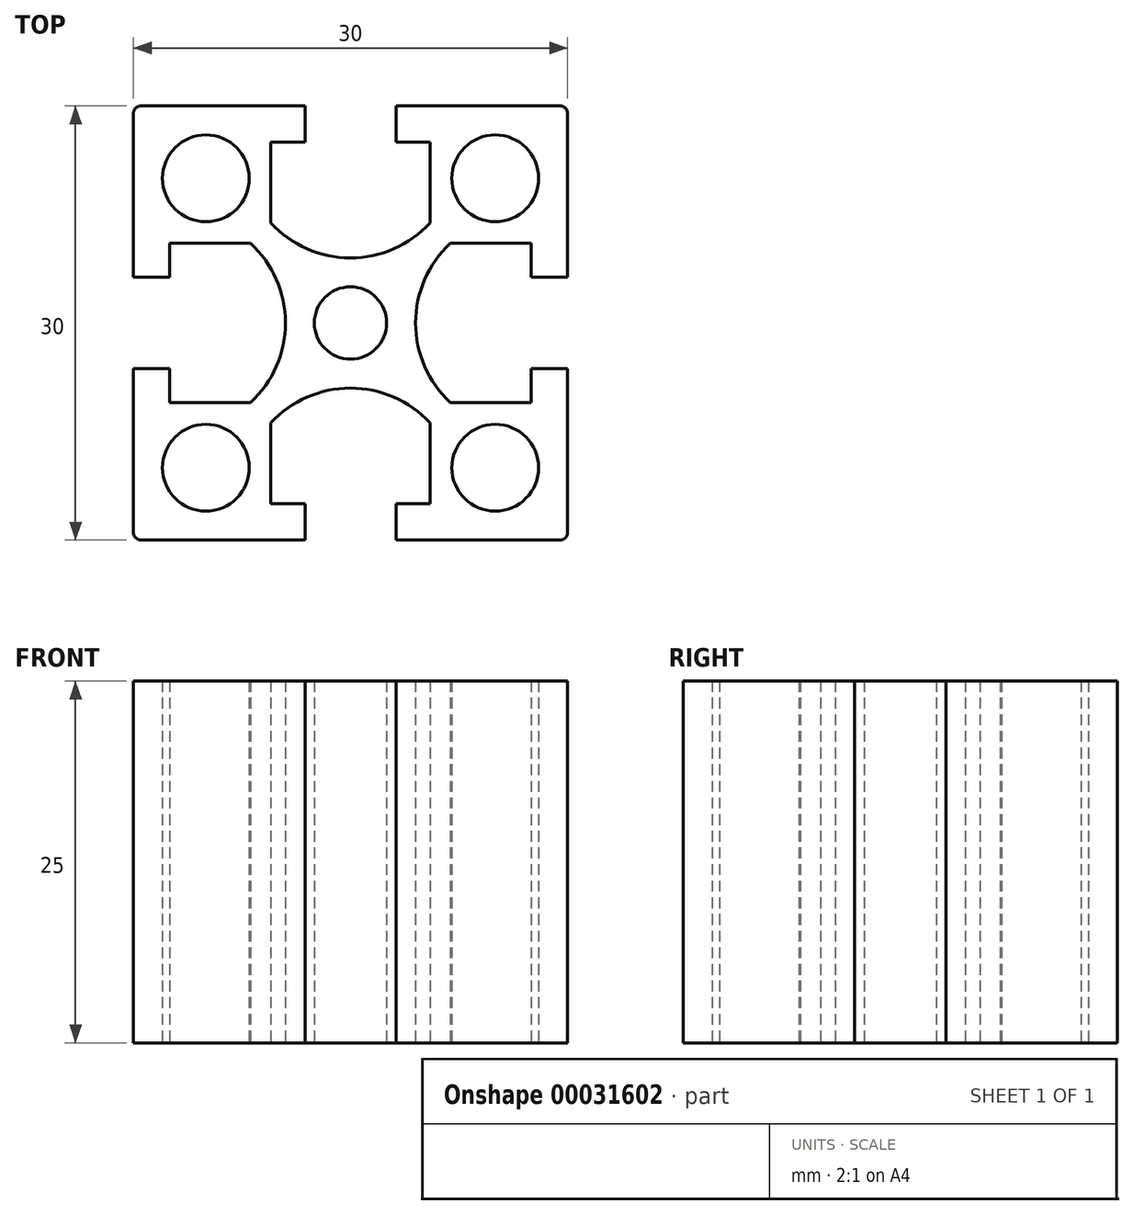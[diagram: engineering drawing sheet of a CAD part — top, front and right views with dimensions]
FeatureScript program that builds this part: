
annotation { "Feature Type Name" : "Feature", "Feature Type Description" : "" }
export const myFeature = defineFeature(function(context is Context, id is Id, definition is map)
    precondition{}
    {
        {
            var Q0;
            Q0=qCreatedBy(makeId("Top.planeOp"),FACE);
            var sketch = newSketch(context, id + "F0", { "sketchPlane" : qUnion([Q0])});
            skCircle(sketch, "E0", {"center": v(0, 0) * mm, "radius": 2.5 * mm});
            skLineSegment(sketch, "E1", {"start": v(0, 0) * mm, "end": v(-15, 0) * mm, "construction": true});
            skLineSegment(sketch, "E2", {"start": v(-15, 0) * mm, "end": v(-15, 15) * mm, "construction": true});
            skLineSegment(sketch, "E3", {"start": v(-15, 15) * mm, "end": v(0, 15) * mm, "construction": true});
            skLineSegment(sketch, "E4", {"start": v(0, 15) * mm, "end": v(0, 0) * mm, "construction": true});
            skLineSegment(sketch, "E5", {"start": v(-15, 15) * mm, "end": v(0, 0) * mm, "construction": true});
            skLineSegment(sketch, "E6", {"start": v(-15, 10) * mm, "end": v(-10, 10) * mm, "construction": true});
            skPoint(sketch, "E7", {"position": v(-15, 3.15) * mm});
            skPoint(sketch, "E8", {"position": v(-15, 5.5) * mm});
            skCircle(sketch, "E9", {"center": v(-10, 10) * mm, "radius": 3 * mm});
            skLineSegment(sketch, "E10", {"start": v(-15, 14.5) * mm, "end": v(-15, 3.15) * mm});
            skLineSegment(sketch, "E11", {"start": v(-15, 3.15) * mm, "end": v(-12.5, 3.15) * mm});
            skLineSegment(sketch, "E12", {"start": v(-12.5, 3.15) * mm, "end": v(-12.5, 5.5) * mm});
            skPoint(sketch, "E13", {"position": v(-4.5, 0) * mm});
            skLineSegment(sketch, "E14", {"start": v(-12.5, 5.5) * mm, "end": v(-5.5, 5.5) * mm, "construction": true});
            skArc(sketch, "E15", {"start": v(-4.5, 0) * mm, "mid": v(-5.13, 3) * mm, "end": v(-6.9, 5.5) * mm});
            skLineSegment(sketch, "E16", {"start": v(-12.5, 5.5) * mm, "end": v(-6.9, 5.5) * mm});
            skLineSegment(sketch, "E17.0.MirrorCS", {"start": v(-14.5, 15) * mm, "end": v(-3.15, 15) * mm});
            skPoint(sketch, "E18.visualSharp", {"position": v(-15, 15) * mm});
            skArc(sketch, "E18.filletArc", {"start": v(-14.5, 15) * mm, "mid": v(-14.85, 14.85) * mm, "end": v(-15, 14.5) * mm});
            skLineSegment(sketch, "E19.0.MirrorCS", {"start": v(-3.15, 15) * mm, "end": v(-3.15, 12.5) * mm});
            skLineSegment(sketch, "E20.0.MirrorCS", {"start": v(-3.15, 12.5) * mm, "end": v(-5.5, 12.5) * mm});
            skLineSegment(sketch, "E21.0.MirrorCS", {"start": v(-5.5, 12.5) * mm, "end": v(-5.5, 6.9) * mm});
            skArc(sketch, "E22.0.MirrorCS", {"start": v(0, 4.5) * mm, "mid": v(-3, 5.13) * mm, "end": v(-5.5, 6.9) * mm});
            skArc(sketch, "E23.0.MirrorCS", {"start": v(-4.5, 0) * mm, "mid": v(-5.13, -3) * mm, "end": v(-6.9, -5.5) * mm});
            skLineSegment(sketch, "E24.0.MirrorCS", {"start": v(-12.5, -5.5) * mm, "end": v(-6.9, -5.5) * mm});
            skLineSegment(sketch, "E25.0.MirrorCS", {"start": v(-12.5, -3.15) * mm, "end": v(-12.5, -5.5) * mm});
            skLineSegment(sketch, "E26.0.MirrorCS", {"start": v(-15, -3.15) * mm, "end": v(-12.5, -3.15) * mm});
            skLineSegment(sketch, "E27.0.MirrorCS", {"start": v(-15, -14.5) * mm, "end": v(-15, -3.15) * mm});
            skArc(sketch, "E28.0.MirrorCS", {"start": v(-14.5, -15) * mm, "mid": v(-14.85, -14.85) * mm, "end": v(-15, -14.5) * mm});
            skLineSegment(sketch, "E29.0.MirrorCS", {"start": v(-14.5, -15) * mm, "end": v(-3.15, -15) * mm});
            skLineSegment(sketch, "E30.0.MirrorCS", {"start": v(-3.15, -15) * mm, "end": v(-3.15, -12.5) * mm});
            skLineSegment(sketch, "E31.0.MirrorCS", {"start": v(-3.15, -12.5) * mm, "end": v(-5.5, -12.5) * mm});
            skLineSegment(sketch, "E32.0.MirrorCS", {"start": v(-5.5, -12.5) * mm, "end": v(-5.5, -6.9) * mm});
            skArc(sketch, "E33.0.MirrorCS", {"start": v(0, -4.5) * mm, "mid": v(-3, -5.13) * mm, "end": v(-5.5, -6.9) * mm});
            skCircle(sketch, "E34.0.MirrorC", {"center": v(-10, -10) * mm, "radius": 3 * mm});
            skArc(sketch, "E35.0.MirrorCS", {"start": v(0, 4.5) * mm, "mid": v(3, 5.13) * mm, "end": v(5.5, 6.9) * mm});
            skLineSegment(sketch, "E36.0.MirrorCS", {"start": v(5.5, 12.5) * mm, "end": v(5.5, 6.9) * mm});
            skLineSegment(sketch, "E37.0.MirrorCS", {"start": v(3.15, 12.5) * mm, "end": v(5.5, 12.5) * mm});
            skLineSegment(sketch, "E38.0.MirrorCS", {"start": v(3.15, 15) * mm, "end": v(3.15, 12.5) * mm});
            skLineSegment(sketch, "E39.0.MirrorCS", {"start": v(14.5, 15) * mm, "end": v(3.15, 15) * mm});
            skArc(sketch, "E40.0.MirrorCS", {"start": v(14.5, 15) * mm, "mid": v(14.85, 14.85) * mm, "end": v(15, 14.5) * mm});
            skLineSegment(sketch, "E41.0.MirrorCS", {"start": v(15, 14.5) * mm, "end": v(15, 3.15) * mm});
            skLineSegment(sketch, "E42.0.MirrorCS", {"start": v(15, 3.15) * mm, "end": v(12.5, 3.15) * mm});
            skLineSegment(sketch, "E43.0.MirrorCS", {"start": v(12.5, 3.15) * mm, "end": v(12.5, 5.5) * mm});
            skLineSegment(sketch, "E44.0.MirrorCS", {"start": v(12.5, 5.5) * mm, "end": v(6.9, 5.5) * mm});
            skArc(sketch, "E45.0.MirrorCS", {"start": v(4.5, 0) * mm, "mid": v(5.13, 3) * mm, "end": v(6.9, 5.5) * mm});
            skArc(sketch, "E46.0.MirrorCS", {"start": v(4.5, 0) * mm, "mid": v(5.13, -3) * mm, "end": v(6.9, -5.5) * mm});
            skLineSegment(sketch, "E47.0.MirrorCS", {"start": v(12.5, -5.5) * mm, "end": v(6.9, -5.5) * mm});
            skLineSegment(sketch, "E48.0.MirrorCS", {"start": v(12.5, -3.15) * mm, "end": v(12.5, -5.5) * mm});
            skLineSegment(sketch, "E49.0.MirrorCS", {"start": v(15, -3.15) * mm, "end": v(12.5, -3.15) * mm});
            skLineSegment(sketch, "E50.0.MirrorCS", {"start": v(15, -14.5) * mm, "end": v(15, -3.15) * mm});
            skArc(sketch, "E51.0.MirrorCS", {"start": v(14.5, -15) * mm, "mid": v(14.85, -14.85) * mm, "end": v(15, -14.5) * mm});
            skLineSegment(sketch, "E52.0.MirrorCS", {"start": v(14.5, -15) * mm, "end": v(3.15, -15) * mm});
            skLineSegment(sketch, "E53.0.MirrorCS", {"start": v(3.15, -15) * mm, "end": v(3.15, -12.5) * mm});
            skLineSegment(sketch, "E54.0.MirrorCS", {"start": v(3.15, -12.5) * mm, "end": v(5.5, -12.5) * mm});
            skLineSegment(sketch, "E55.0.MirrorCS", {"start": v(5.5, -12.5) * mm, "end": v(5.5, -6.9) * mm});
            skArc(sketch, "E56.0.MirrorCS", {"start": v(0, -4.5) * mm, "mid": v(3, -5.13) * mm, "end": v(5.5, -6.9) * mm});
            skCircle(sketch, "E57.0.MirrorC", {"center": v(10, 10) * mm, "radius": 3 * mm});
            skCircle(sketch, "E58.0.MirrorC", {"center": v(10, -10) * mm, "radius": 3 * mm});
            skSolve(sketch);
        }
        {
            var Q0;
            Q0=makeQuery(id+"F0.imprint","IMPRINT",FACE,{"disambiguationData":[TD([[makeQuery(id+"F0.imprint","IMPRINT",EDGE,{"derivedFrom":sQuery(id+"F0.wireOp",EDGE,"E0")}),-1.0]])]});
            extrude(context, id + "F1", {"entities" : qUnion([Q0]), "depth" : 25 * mm});
        }
    });
